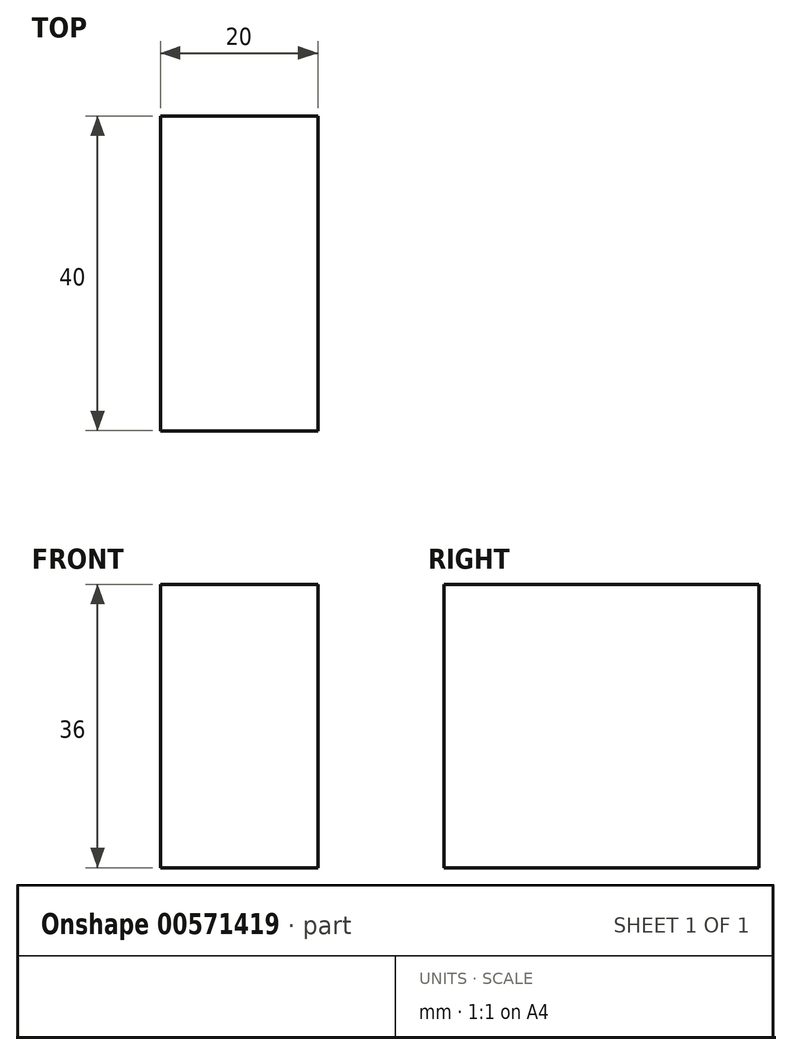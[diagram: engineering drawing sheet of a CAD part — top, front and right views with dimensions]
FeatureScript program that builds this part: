
annotation { "Feature Type Name" : "Feature", "Feature Type Description" : "" }
export const myFeature = defineFeature(function(context is Context, id is Id, definition is map)
    precondition{}
    {
        {
            var Q0;
            Q0=qCreatedBy(makeId("Top.planeOp"),FACE);
            var sketch = newSketch(context, id + "F0", { "sketchPlane" : qUnion([Q0])});
            skLineSegment(sketch, "E0.bottom", {"start": v(9.5, 23.07) * mm, "end": v(-10.5, 23.07) * mm});
            skLineSegment(sketch, "E0.top", {"start": v(9.5, -16.93) * mm, "end": v(-10.5, -16.93) * mm});
            skLineSegment(sketch, "E0.left", {"start": v(9.5, 23.07) * mm, "end": v(9.5, -16.93) * mm});
            skLineSegment(sketch, "E0.right", {"start": v(-10.5, 23.07) * mm, "end": v(-10.5, -16.93) * mm});
            skSolve(sketch);
        }
        {
            var Q0;
            Q0=makeQuery(id+"F0.imprint","IMPRINT",FACE,{"disambiguationData":[TD([[makeQuery(id+"F0.imprint","IMPRINT",EDGE,{"derivedFrom":sQuery(id+"F0.wireOp",EDGE,"E0.bottom")}),1.0]])]});
            extrude(context, id + "F1", {"entities" : qUnion([Q0]), "depth" : 36 * mm, "offsetDistance" : 25 * mm});
        }
    });
